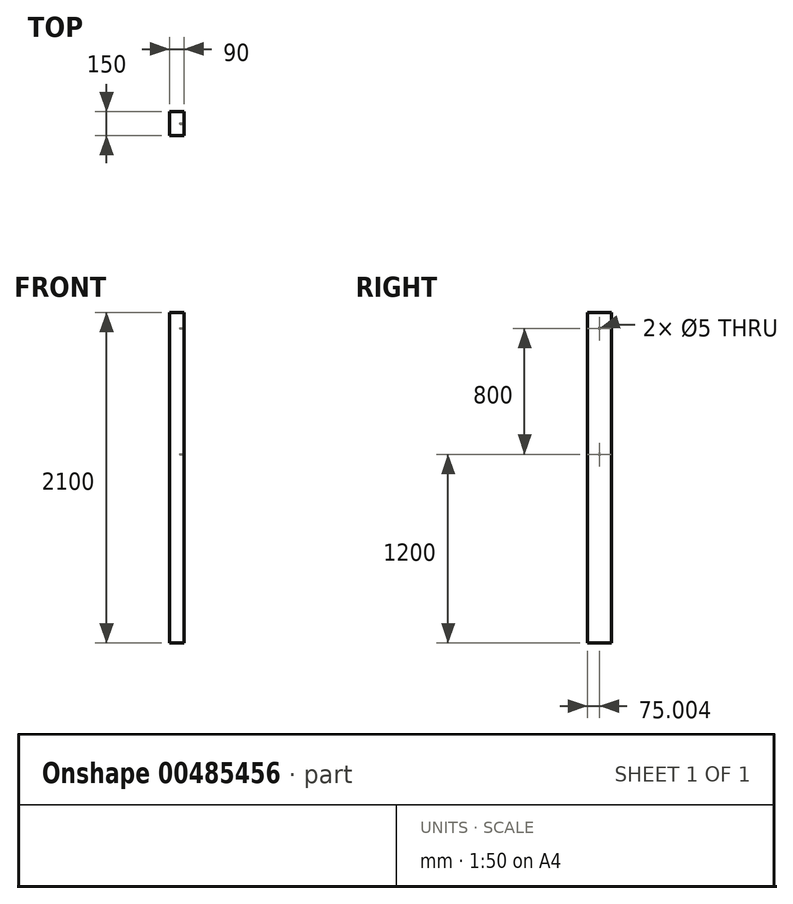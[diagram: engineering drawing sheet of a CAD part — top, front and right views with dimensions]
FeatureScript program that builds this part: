
annotation { "Feature Type Name" : "Feature", "Feature Type Description" : "" }
export const myFeature = defineFeature(function(context is Context, id is Id, definition is map)
    precondition{}
    {
        {
            var Q0;
            Q0=qCreatedBy(makeId("Top.planeOp"),FACE);
            var sketch = newSketch(context, id + "F0", { "sketchPlane" : qUnion([Q0])});
            skLineSegment(sketch, "E0.bottom", {"start": v(-45, 141.65) * mm, "end": v(45, 141.65) * mm});
            skLineSegment(sketch, "E0.top", {"start": v(-45, -8.35) * mm, "end": v(45, -8.35) * mm});
            skLineSegment(sketch, "E0.left", {"start": v(-45, 141.65) * mm, "end": v(-45, -8.35) * mm});
            skLineSegment(sketch, "E0.right", {"start": v(45, 141.65) * mm, "end": v(45, -8.35) * mm});
            skPoint(sketch, "E0.middle", {"position": v(0, 66.65) * mm});
            skLineSegment(sketch, "E1.bottom", {"start": v(34.26, 141.65) * mm, "end": v(-34.26, 141.65) * mm});
            skLineSegment(sketch, "E1.top", {"start": v(34.26, 141.65) * mm, "end": v(-34.26, 141.65) * mm});
            skLineSegment(sketch, "E1.left", {"start": v(34.26, 141.65) * mm, "end": v(34.26, 141.65) * mm});
            skLineSegment(sketch, "E1.right", {"start": v(-34.26, 141.65) * mm, "end": v(-34.26, 141.65) * mm});
            skPoint(sketch, "E1.middle", {"position": v(0, 141.65) * mm});
            skSolve(sketch);
        }
        {
            var Q0;
            Q0=makeQuery(id+"F0.imprint","IMPRINT",FACE,{"disambiguationData":[TD([[makeQuery(id+"F0.imprint","IMPRINT",EDGE,{"derivedFrom":sQuery(id+"F0.wireOp",EDGE,"E0.top")}),1.0]])]});
            extrude(context, id + "F1", {"entities" : qUnion([Q0]), "depth" : 2100 * mm});
        }
        {
            var Q0;
            Q0=makeQuery(id+"F1.opExtrude","SWEPT_FACE",FACE,{"disambiguationData":[OSD([sQuery(id+"F0.wireOp",EDGE,"E0.right")])]});
            var sketch = newSketch(context, id + "F2", { "sketchPlane" : qUnion([Q0])});
            skPoint(sketch, "E2", {"position": v(66.65, 1200) * mm});
            skPoint(sketch, "E3", {"position": v(66.65, 2000) * mm});
            skSolve(sketch);
        }
        {
            var Q0;
            Q0=sQuery(id+"F2.wireOp",VERTEX,"E2");
            var Q1;
            Q1=makeQuery(id+"F1.opExtrude","SWEPT_BODY",BODY,{"disambiguationData":[OSD([sQuery(id+"F0.wireOp",EDGE,"E0.bottom"),sQuery(id+"F0.wireOp",EDGE,"E0.top"),sQuery(id+"F0.wireOp",EDGE,"E0.left"),sQuery(id+"F0.wireOp",EDGE,"E0.right"),sQuery(id+"F0.wireOp",EDGE,"E1.top")])]});
            hole(context, id + "F3", {"style" : HoleStyle.SIMPLE, "endStyle" : HoleEndStyle.BLIND, "holeDiameter" : 5 * mm, "holeDepth" : 25 * mm, "isTappedThrough" : true, "tappedDepth" : 12 * mm, "tapClearance" : 3, "locations" : qUnion([Q0]), "scope" : qUnion([Q1])});
        }
        {
            var Q0;
            Q0=sQuery(id+"F2.wireOp",VERTEX,"E3");
            var Q1;
            Q1=makeQuery(id+"F1.opExtrude","SWEPT_BODY",BODY,{"disambiguationData":[OSD([sQuery(id+"F0.wireOp",EDGE,"E0.bottom"),sQuery(id+"F0.wireOp",EDGE,"E0.top"),sQuery(id+"F0.wireOp",EDGE,"E0.left"),sQuery(id+"F0.wireOp",EDGE,"E0.right"),sQuery(id+"F0.wireOp",EDGE,"E1.top")])]});
            hole(context, id + "F4", {"style" : HoleStyle.SIMPLE, "endStyle" : HoleEndStyle.BLIND, "holeDiameter" : 5 * mm, "holeDepth" : 25 * mm, "isTappedThrough" : true, "tappedDepth" : 12 * mm, "tapClearance" : 3, "locations" : qUnion([Q0]), "scope" : qUnion([Q1])});
        }
    });
